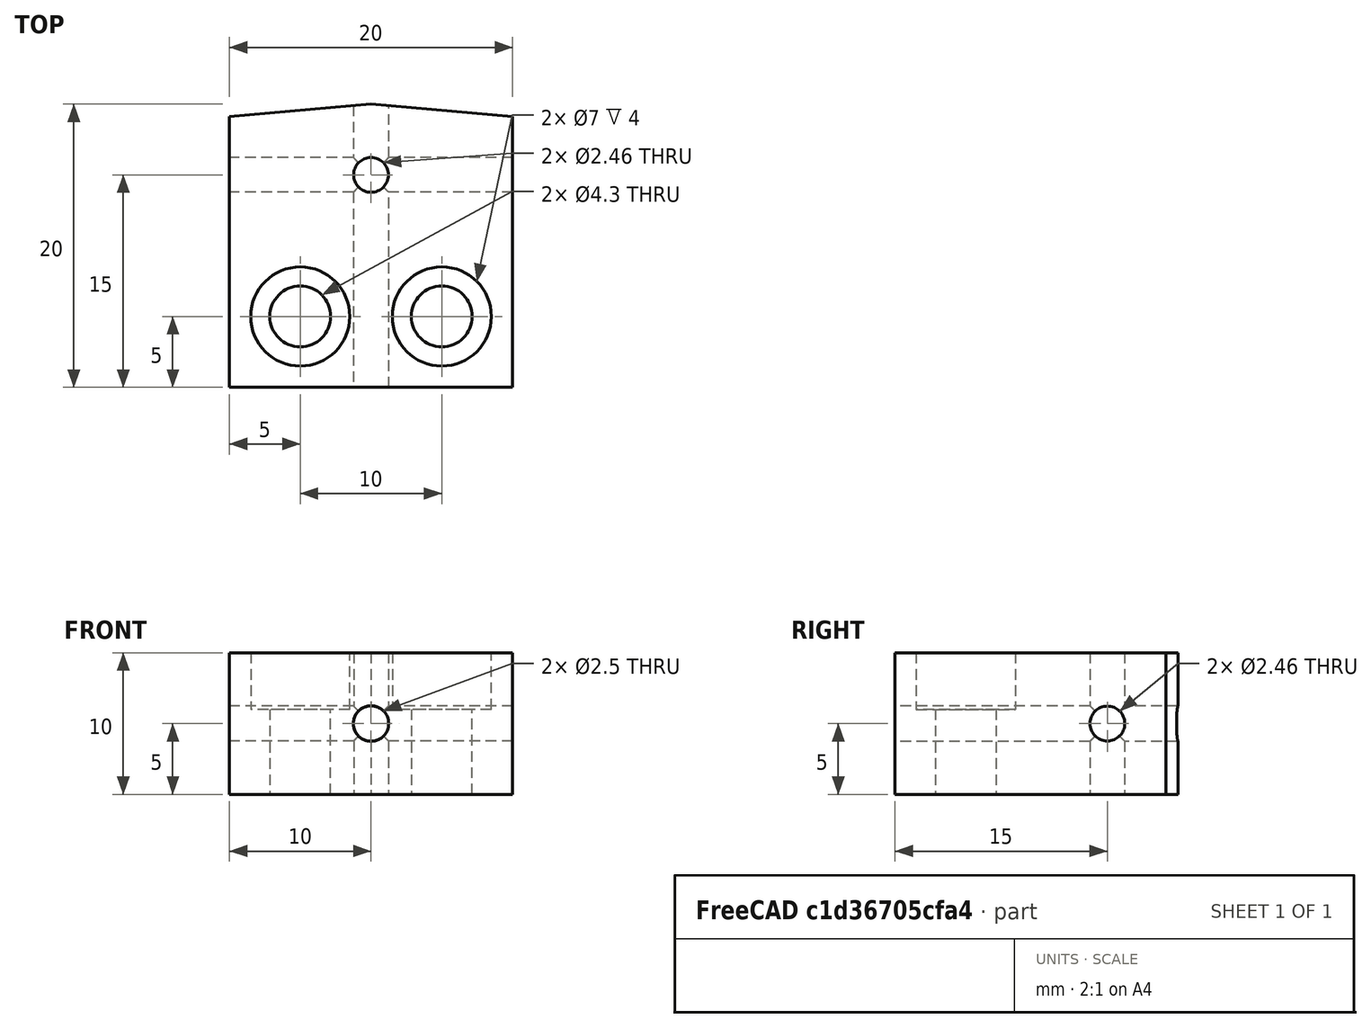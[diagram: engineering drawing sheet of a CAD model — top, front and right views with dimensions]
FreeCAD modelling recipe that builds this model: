
FCSTD DOCUMENT  (FreeCAD 0.21R0.21.2)
Label: StaticFiberFerruleMount_M4
License: All rights reserved
LicenseURL: https://en.wikipedia.org/wiki/All_rights_reserved
objects: TechDraw::DrawViewDimension×23, Part::Cylinder×5, Part::Cut×5, TechDraw::DrawProjGroupItem×5, Part::MultiFuse×4, Part::Box×3, TechDraw::DrawViewPart×3, TechDraw::DrawViewSection×3, Part::FeaturePython×2, TechDraw::DrawSVGTemplate×2, TechDraw::DrawPage×2, Part::Compound×1, TechDraw::DrawProjGroup×1
note: 56 computed .brp shape members not serialized (recipe doc carries the construction recipe); baked Part::Feature solids carry a one-line shape summary decoded from their .brp

FEATURE [Part::Box] Box  label="Cube"
  AttacherType = Attacher::AttachEngine3D
  Height = 10
  Length = 20
  Placement = pos=(-10,0,0) rot=(0,0,1;0rad)
  Width = 20
FEATURE [Part::Cylinder] Cylinder
  Angle = 360
  AttacherType = Attacher::AttachEngine3D
  FirstAngle = 0
  Height = 4
  Placement = pos=(0,0,6) rot=(0,0,1;0rad)
  Radius = 3.5
  SecondAngle = 0
FEATURE [Part::Cylinder] Cylinder001
  Angle = 360
  AttacherType = Attacher::AttachEngine3D
  FirstAngle = 0
  Height = 10
  Radius = 2.15
  SecondAngle = 0
FEATURE [Part::MultiFuse] Fusion
  Placement = pos=(-5,5,0) rot=(0,0,1;0rad)
  Shapes = -> [Cylinder001,Cylinder]
FEATURE [Part::Cylinder] Cylinder002
  Angle = 360
  AttacherType = Attacher::AttachEngine3D
  FirstAngle = 0
  Height = 4
  Placement = pos=(0,0,6) rot=(0,0,1;0rad)
  Radius = 3.5
  SecondAngle = 0
FEATURE [Part::Cylinder] Cylinder003
  Angle = 360
  AttacherType = Attacher::AttachEngine3D
  FirstAngle = 0
  Height = 10
  Radius = 2.15
  SecondAngle = 0
FEATURE [Part::MultiFuse] Fusion001
  Placement = pos=(5,5,0) rot=(0,0,1;0rad)
  Shapes = -> [Cylinder003,Cylinder002]
FEATURE [Part::MultiFuse] Fusion002
  Shapes = -> [Fusion,Fusion001]
FEATURE [Part::Cut] Cut
  Base = -> Box
  Tool = -> Fusion002
FEATURE [Part::Cylinder] Cylinder004
  Angle = 360
  AttacherType = Attacher::AttachEngine3D
  FirstAngle = 0
  Height = 20
  Placement = pos=(0,0,5) rot=(1,0,0;-1.5708rad)
  Radius = 1.25
  SecondAngle = 0
FEATURE [Part::Cut] Cut001
  Base = -> Cut
  Tool = -> Cylinder004
FEATURE [Part::FeaturePython] ScrewTap  label="M3x20-ScrewTap"  # Fasteners workbench fastener (typed FeaturePython)
  Placement = pos=(10,15,5) rot=(0,1,0;1.5708rad)
  diameter = 4
  diameterCustom = 20
  invert = false
  leftHanded = false
  length = 20
  matchOuter = false
  offset = 0
  pitchCustom = 1
  thread = false
  type = 2
FEATURE [Part::FeaturePython] ScrewTap001  label="M3x20-ScrewTap001"  # Fasteners workbench fastener (typed FeaturePython)
  Placement = pos=(0,15,15) rot=(0,1,0;0rad)
  diameter = 4
  diameterCustom = 20
  invert = false
  leftHanded = false
  length = 20
  matchOuter = false
  offset = 0
  pitchCustom = 1
  thread = false
  type = 2
FEATURE [Part::Cut] Cut002
  Base = -> Cut001
  Tool = -> ScrewTap
FEATURE [Part::Cut] Cut003
  Base = -> Cut002
  Tool = -> ScrewTap001
FEATURE [Part::Box] Box001  label="Cube001"
  AttacherType = Attacher::AttachEngine3D
  Height = 10
  Length = 15
  Placement = pos=(0,20,0) rot=(0,0,1;-0.087266rad)
  Width = 5
FEATURE [Part::Box] Box002  label="Cube002"
  AttacherType = Attacher::AttachEngine3D
  Height = 10
  Length = 15
  Placement = pos=(0,20,0) rot=(0,0,-1;0.087266rad)
  Width = 5
FEATURE [Part::Compound] Compound
  Links = -> [Box002]
  Placement = pos=(0,0,10) rot=(0,1,0;3.14159rad)
FEATURE [Part::MultiFuse] Fusion003
  Shapes = -> [Compound,Box001]
FEATURE [Part::Cut] Cut004  label="FiberMount"
  Base = -> Cut003
  Tool = -> Fusion003
FEATURE [TechDraw::DrawSVGTemplate] Template
  EditableTexts = Designed_by_Name=Thomas Spielauer; FC-Date=2024-01-30; FC-SC=mm; FC-Title=M4 Fiber Mount; Subtitle=For 2.5mm Ferrules
  Height = 210
  Orientation = 1
  Template = <path>
  Width = 297
FEATURE [TechDraw::DrawProjGroupItem] ProjItem  label="Front"
  CoarseView = false
  Direction = (0,0,1)
  Focus = 100
  HardHidden = false
  IsoCount = 0
  IsoHidden = false
  IsoVisible = false
  LockPosition = true
  Perspective = false
  Rotation = 0
  RotationVector = (-1,0,0)
  Scale = 2.5
  ScaleType = 2
  ScrubCount = 0
  SeamHidden = false
  SeamVisible = false
  SmoothHidden = false
  SmoothVisible = true
  Source = -> [Cut004]
  Type = 0
  X = 0
  XDirection = (-1,0,0)
  Y = 0
FEATURE [TechDraw::DrawProjGroupItem] ProjItem001  label="Left"
  CoarseView = false
  Direction = (1,0,1e-16)
  Focus = 100
  HardHidden = false
  IsoCount = 0
  IsoHidden = false
  IsoVisible = false
  LockPosition = false
  Perspective = false
  Rotation = 0
  RotationVector = (1,0,0)
  Scale = 2.5
  ScaleType = 2
  ScrubCount = 0
  SeamHidden = false
  SeamVisible = false
  SmoothHidden = false
  SmoothVisible = true
  Source = -> [Cut004]
  Type = 1
  X = 83.8051
  XDirection = (-1e-16,0,1)
  Y = 0
FEATURE [TechDraw::DrawProjGroupItem] ProjItem002  label="Rear"
  CoarseView = false
  Direction = (0,0,-1)
  Focus = 100
  HardHidden = false
  IsoCount = 0
  IsoHidden = false
  IsoVisible = false
  LockPosition = false
  Perspective = false
  Rotation = 0
  RotationVector = (1,0,0)
  Scale = 2.5
  ScaleType = 2
  ScrubCount = 0
  SeamHidden = false
  SeamVisible = false
  SmoothHidden = false
  SmoothVisible = true
  Source = -> [Cut004]
  Type = 3
  X = 176.998
  XDirection = (1,0,0)
  Y = 0
FEATURE [TechDraw::DrawProjGroupItem] ProjItem003  label="Top"
  CoarseView = false
  Direction = (0,-1,0)
  Focus = 100
  HardHidden = false
  IsoCount = 0
  IsoHidden = false
  IsoVisible = false
  LockPosition = false
  Perspective = false
  Rotation = 0
  RotationVector = (1,0,0)
  Scale = 2.5
  ScaleType = 2
  ScrubCount = 0
  SeamHidden = false
  SeamVisible = false
  SmoothHidden = false
  SmoothVisible = true
  Source = -> [Cut004]
  Type = 4
  X = 0
  XDirection = (-1,0,0)
  Y = -69.8299
FEATURE [TechDraw::DrawProjGroupItem] ProjItem004  label="Bottom"
  CoarseView = false
  Direction = (0,1,0)
  Focus = 100
  HardHidden = false
  IsoCount = 0
  IsoHidden = false
  IsoVisible = false
  LockPosition = false
  Perspective = false
  Rotation = 0
  RotationVector = (1,0,0)
  Scale = 2.5
  ScaleType = 2
  ScrubCount = 0
  SeamHidden = false
  SeamVisible = false
  SmoothHidden = false
  SmoothVisible = true
  Source = -> [Cut004]
  Type = 5
  X = 0
  XDirection = (-1,0,0)
  Y = 66.0072
FEATURE [TechDraw::DrawProjGroup] ProjGroup
  Anchor = -> ProjItem
  AutoDistribute = false
  LockPosition = false
  ProjectionType = 0
  Rotation = 0
  Scale = 2.5
  ScaleType = 2
  Source = -> [Cut004]
  Views = -> [ProjItem,ProjItem001,ProjItem002,ProjItem003,ProjItem004]
  X = 63.5172
  Y = 109.729
  spacingX = 15
  spacingY = 15
FEATURE [TechDraw::DrawViewDimension] Dimension
  AngleOverride = false
  Arbitrary = false
  ArbitraryTolerances = false
  EqualTolerance = true
  ExtensionAngle = 0
  FormatSpec = %.2w
  FormatSpecOverTolerance = %+.2w
  FormatSpecUnderTolerance = %+.2w
  Inverted = false
  LineAngle = 0
  LockPosition = false
  MeasureType = 1
  OverTolerance = 0
  References2D = -> [ProjItem002]
  Rotation = 0
  ScaleType = 0
  TheoreticalExact = false
  Type = 1
  UnderTolerance = 0
  X = -1.08718
  Y = 38.276
FEATURE [TechDraw::DrawViewDimension] Dimension001
  AngleOverride = false
  Arbitrary = false
  ArbitraryTolerances = false
  EqualTolerance = true
  ExtensionAngle = 0
  FormatSpec = %.2w
  FormatSpecOverTolerance = %+.2w
  FormatSpecUnderTolerance = %+.2w
  Inverted = false
  LineAngle = 0
  LockPosition = false
  MeasureType = 1
  OverTolerance = 0
  References2D = -> [ProjItem002]
  Rotation = 0
  ScaleType = 0
  TheoreticalExact = false
  Type = 2
  UnderTolerance = 0
  X = 33.6541
  Y = 3.92646
FEATURE [TechDraw::DrawViewDimension] Dimension002
  AngleOverride = false
  Arbitrary = false
  ArbitraryTolerances = false
  EqualTolerance = true
  ExtensionAngle = 0
  FormatSpec = %.2w
  FormatSpecOverTolerance = %+.2w
  FormatSpecUnderTolerance = %+.2w
  Inverted = false
  LineAngle = 0
  LockPosition = false
  MeasureType = 1
  OverTolerance = 0
  References2D = -> [ProjItem002]
  Rotation = 0
  ScaleType = 0
  TheoreticalExact = false
  Type = 1
  UnderTolerance = 0
  X = -19.3984
  Y = 49.6787
FEATURE [TechDraw::DrawViewDimension] Dimension003
  AngleOverride = false
  Arbitrary = false
  ArbitraryTolerances = false
  EqualTolerance = true
  ExtensionAngle = 0
  FormatSpec = %.2w
  FormatSpecOverTolerance = %+.2w
  FormatSpecUnderTolerance = %+.2w
  Inverted = false
  LineAngle = 0
  LockPosition = false
  MeasureType = 1
  OverTolerance = 0
  References2D = -> [ProjItem002]
  Rotation = 0
  ScaleType = 0
  TheoreticalExact = false
  Type = 1
  UnderTolerance = 0
  X = 18.4123
  Y = 48.3541
FEATURE [TechDraw::DrawViewDimension] Dimension004
  AngleOverride = false
  Arbitrary = false
  ArbitraryTolerances = false
  EqualTolerance = true
  ExtensionAngle = 0
  FormatSpec = %.2w
  FormatSpecOverTolerance = %+.2w
  FormatSpecUnderTolerance = %+.2w
  Inverted = false
  LineAngle = 0
  LockPosition = false
  MeasureType = 1
  OverTolerance = 0
  References2D = -> [ProjItem002]
  Rotation = 0
  ScaleType = 0
  TheoreticalExact = false
  Type = 2
  UnderTolerance = 0
  X = -36.9072
  Y = 21.9842
FEATURE [TechDraw::DrawViewDimension] Dimension005
  AngleOverride = false
  Arbitrary = false
  ArbitraryTolerances = false
  EqualTolerance = true
  ExtensionAngle = 0
  FormatSpec = %.2w
  FormatSpecOverTolerance = %+.2w
  FormatSpecUnderTolerance = %+.2w
  Inverted = false
  LineAngle = 0
  LockPosition = false
  MeasureType = 1
  OverTolerance = 0
  References2D = -> [ProjItem002]
  Rotation = 0
  ScaleType = 0
  TheoreticalExact = false
  Type = 2
  UnderTolerance = 0
  X = -49.4824
  Y = 5.98178
FEATURE [TechDraw::DrawViewDimension] Dimension006
  AngleOverride = false
  Arbitrary = false
  ArbitraryTolerances = false
  EqualTolerance = true
  ExtensionAngle = 0
  FormatSpec = %.2w
  FormatSpecOverTolerance = %+.2w
  FormatSpecUnderTolerance = %+.2w
  Inverted = false
  LineAngle = 0
  LockPosition = false
  MeasureType = 1
  OverTolerance = 0
  References2D = -> [ProjItem001]
  Rotation = 0
  ScaleType = 0
  TheoreticalExact = false
  Type = 2
  UnderTolerance = 0
  X = 20.9282
  Y = -0.08017
FEATURE [TechDraw::DrawViewDimension] Dimension007
  AngleOverride = false
  Arbitrary = false
  ArbitraryTolerances = false
  EqualTolerance = true
  ExtensionAngle = 0
  FormatSpec = %.2w
  FormatSpecOverTolerance = %+.2w
  FormatSpecUnderTolerance = %+.2w
  Inverted = false
  LineAngle = 0
  LockPosition = false
  MeasureType = 1
  OverTolerance = 0
  References2D = -> [ProjItem001]
  Rotation = 0
  ScaleType = 0
  TheoreticalExact = false
  Type = 1
  UnderTolerance = 0
  X = 1.11941
  Y = 39.7819
FEATURE [TechDraw::DrawViewDimension] Dimension008
  AngleOverride = false
  Arbitrary = false
  ArbitraryTolerances = false
  EqualTolerance = true
  ExtensionAngle = 0
  FormatSpec = %.2w
  FormatSpecOverTolerance = %+.2w
  FormatSpecUnderTolerance = %+.2w
  Inverted = false
  LineAngle = 0
  LockPosition = false
  MeasureType = 1
  OverTolerance = 0
  References2D = -> [ProjItem]
  Rotation = 0
  ScaleType = 0
  TheoreticalExact = false
  Type = 6
  UnderTolerance = 0
  X = 17.4114
  Y = -11.6712
FEATURE [TechDraw::DrawViewDimension] Dimension009
  AngleOverride = false
  Arbitrary = false
  ArbitraryTolerances = false
  EqualTolerance = true
  ExtensionAngle = 0
  FormatSpec = ⌀%.2w
  FormatSpecOverTolerance = %+.2w
  FormatSpecUnderTolerance = %+.2w
  Inverted = false
  LineAngle = 0
  LockPosition = false
  MeasureType = 1
  OverTolerance = 0
  References2D = -> [ProjItem]
  Rotation = 0
  ScaleType = 0
  TheoreticalExact = false
  Type = 5
  UnderTolerance = 0
  X = 34.847
  Y = 32.1835
FEATURE [TechDraw::DrawViewDimension] Dimension010
  AngleOverride = false
  Arbitrary = false
  ArbitraryTolerances = false
  EqualTolerance = true
  ExtensionAngle = 0
  FormatSpec = ⌀%.2w
  FormatSpecOverTolerance = %+.2w
  FormatSpecUnderTolerance = %+.2w
  Inverted = false
  LineAngle = 0
  LockPosition = false
  MeasureType = 1
  OverTolerance = 0
  References2D = -> [ProjItem]
  Rotation = 0
  ScaleType = 0
  TheoreticalExact = false
  Type = 5
  UnderTolerance = 0
  X = 42.735
  Y = 24.4512
FEATURE [TechDraw::DrawViewDimension] Dimension011
  AngleOverride = false
  Arbitrary = false
  ArbitraryTolerances = false
  EqualTolerance = true
  ExtensionAngle = 0
  FormatSpec = ⌀%.2w
  FormatSpecOverTolerance = %+.2w
  FormatSpecUnderTolerance = %+.2w
  Inverted = false
  LineAngle = 0
  LockPosition = false
  MeasureType = 1
  OverTolerance = 0
  References2D = -> [ProjItem003]
  Rotation = 0
  ScaleType = 0
  TheoreticalExact = false
  Type = 5
  UnderTolerance = 0
  X = 36.0608
  Y = 7.78296
FEATURE [TechDraw::DrawViewDimension] Dimension012
  AngleOverride = false
  Arbitrary = false
  ArbitraryTolerances = false
  EqualTolerance = true
  ExtensionAngle = 0
  FormatSpec = ⌀%.2w (M3)
  FormatSpecOverTolerance = %+.2w
  FormatSpecUnderTolerance = %+.2w
  Inverted = false
  LineAngle = 0
  LockPosition = false
  MeasureType = 1
  OverTolerance = 0
  References2D = -> [ProjItem]
  Rotation = 0
  ScaleType = 0
  TheoreticalExact = false
  Type = 5
  UnderTolerance = 0
  X = 47.6967
  Y = -20.8245
FEATURE [TechDraw::DrawViewDimension] Dimension013
  AngleOverride = false
  Arbitrary = false
  ArbitraryTolerances = false
  EqualTolerance = true
  ExtensionAngle = 0
  FormatSpec = ⌀%.2w (M3)
  FormatSpecOverTolerance = %+.2w
  FormatSpecUnderTolerance = %+.2w
  Inverted = false
  LineAngle = 0
  LockPosition = false
  MeasureType = 1
  OverTolerance = 0
  References2D = -> [ProjItem001]
  Rotation = 0
  ScaleType = 0
  TheoreticalExact = false
  Type = 5
  UnderTolerance = 0
  X = -33.134
  Y = 3.74181
FEATURE [TechDraw::DrawViewDimension] Dimension014
  AngleOverride = false
  Arbitrary = false
  ArbitraryTolerances = false
  EqualTolerance = true
  ExtensionAngle = 0
  FormatSpec = %.2w
  FormatSpecOverTolerance = %+.2w
  FormatSpecUnderTolerance = %+.2w
  Inverted = false
  LineAngle = 0
  LockPosition = false
  MeasureType = 1
  OverTolerance = 0
  References2D = -> [ProjItem004]
  Rotation = 0
  ScaleType = 0
  TheoreticalExact = false
  Type = 1
  UnderTolerance = 0
  X = 10.9437
  Y = -18.4908
FEATURE [TechDraw::DrawPage] Page
  KeepUpdated = true
  NextBalloonIndex = 1
  ProjectionType = 0
  Template = -> Template
  Views = -> [ProjGroup,Dimension,Dimension001,Dimension002,Dimension003,Dimension004,Dimension005,Dimension006,Dimension007,Dimension008,Dimension009,Dimension010,Dimension011,Dimension012,Dimension013,Dimension014]
FEATURE [TechDraw::DrawSVGTemplate] Template001
  EditableTexts = Designed_by_Name=Thomas Spielauer; FC-Date=2024-01-30; FC-SC=mm; FC-SH=2/2; FC-Title=M4 Fiber Mount; Subtitle=For 2.5mm fiber ferrules
  Height = 210
  Orientation = 1
  Template = <path>
  Width = 297
FEATURE [TechDraw::DrawViewPart] View
  CoarseView = false
  Direction = (0,0,1)
  Focus = 100
  HardHidden = false
  IsoCount = 0
  IsoHidden = false
  IsoVisible = false
  LockPosition = false
  Perspective = false
  Rotation = 0
  Scale = 2
  ScaleType = 2
  ScrubCount = 0
  SeamHidden = false
  SeamVisible = false
  SmoothHidden = false
  SmoothVisible = true
  Source = -> [Cut004]
  X = 49.0155
  XDirection = (-1,0,0)
  Y = 162
FEATURE [TechDraw::DrawViewSection] SectionView  label="Section  - "
  BaseView = -> View
  CoarseView = false
  CutSurfaceDisplay = 2
  Direction = (1,1e-16,0)
  FileGeomPattern = <path>
  FileHatchPattern = <path>
  Focus = 100
  FuseBeforeCut = false
  HardHidden = false
  HatchOffset = (0,0,0)
  HatchRotation = 0
  HatchScale = 1
  IsoCount = 0
  IsoHidden = false
  IsoVisible = false
  LockPosition = false
  NameGeomPattern = Diamond
  Perspective = false
  Rotation = -90
  Scale = 2
  ScaleType = 2
  ScrubCount = 0
  SeamHidden = false
  SeamVisible = false
  SectionDirection = 4
  SectionNormal = (1,1e-16,0)
  SectionOrigin = (0,10,5)
  SmoothHidden = false
  SmoothVisible = true
  Source = -> [Cut004]
  TrimAfterCut = false
  X = 98.3829
  XDirection = (-1e-16,1,0)
  Y = 161.597
FEATURE [TechDraw::DrawViewPart] View001
  CoarseView = false
  Direction = (0,0,1)
  Focus = 100
  HardHidden = false
  IsoCount = 0
  IsoHidden = false
  IsoVisible = false
  LockPosition = false
  Perspective = false
  Rotation = 0
  Scale = 2
  ScaleType = 2
  ScrubCount = 0
  SeamHidden = false
  SeamVisible = false
  SmoothHidden = false
  SmoothVisible = true
  Source = -> [Cut004]
  X = 168.995
  XDirection = (-1,0,0)
  Y = 161.465
FEATURE [TechDraw::DrawViewSection] SectionView001  label="Section  - 001"
  BaseView = -> View001
  CoarseView = false
  CutSurfaceDisplay = 2
  Direction = (1,1e-16,0)
  FileGeomPattern = <path>
  FileHatchPattern = <path>
  Focus = 100
  FuseBeforeCut = false
  HardHidden = false
  HatchOffset = (0,0,0)
  HatchRotation = 0
  HatchScale = 1
  IsoCount = 0
  IsoHidden = false
  IsoVisible = false
  LockPosition = false
  NameGeomPattern = Diamond
  Perspective = false
  Rotation = -90
  Scale = 2
  ScaleType = 2
  ScrubCount = 0
  SeamHidden = false
  SeamVisible = false
  SectionDirection = 4
  SectionNormal = (1,1e-16,0)
  SectionOrigin = (5,10,5)
  SmoothHidden = false
  SmoothVisible = true
  Source = -> [Cut004]
  TrimAfterCut = false
  X = 225.041
  XDirection = (-1e-16,1,0)
  Y = 158.119
FEATURE [TechDraw::DrawViewDimension] Dimension015
  AngleOverride = false
  Arbitrary = false
  ArbitraryTolerances = false
  EqualTolerance = true
  ExtensionAngle = 0
  FormatSpec = %.2w
  FormatSpecOverTolerance = %+.2w
  FormatSpecUnderTolerance = %+.2w
  Inverted = false
  LineAngle = 0
  LockPosition = false
  MeasureType = 1
  OverTolerance = 0
  References2D = -> [SectionView]
  Rotation = 0
  ScaleType = 0
  TheoreticalExact = false
  Type = 1
  UnderTolerance = 0
  X = 9.95348
  Y = -24.9456
FEATURE [TechDraw::DrawViewDimension] Dimension016
  AngleOverride = false
  Arbitrary = false
  ArbitraryTolerances = false
  EqualTolerance = true
  ExtensionAngle = 0
  FormatSpec = %.2w (M3)
  FormatSpecOverTolerance = %+.2w
  FormatSpecUnderTolerance = %+.2w
  Inverted = false
  LineAngle = 0
  LockPosition = false
  MeasureType = 1
  OverTolerance = 0
  References2D = -> [SectionView]
  Rotation = 0
  ScaleType = 0
  TheoreticalExact = false
  Type = 2
  UnderTolerance = 0
  X = 17.8961
  Y = 1.78628
FEATURE [TechDraw::DrawViewDimension] Dimension017
  AngleOverride = false
  Arbitrary = false
  ArbitraryTolerances = false
  EqualTolerance = true
  ExtensionAngle = 0
  FormatSpec = %.2w
  FormatSpecOverTolerance = %+.2w
  FormatSpecUnderTolerance = %+.2w
  Inverted = false
  LineAngle = 0
  LockPosition = false
  MeasureType = 1
  OverTolerance = 0
  References2D = -> [SectionView001]
  Rotation = 0
  ScaleType = 0
  TheoreticalExact = false
  Type = 2
  UnderTolerance = 0
  X = 19.2955
  Y = 12.763
FEATURE [TechDraw::DrawViewDimension] Dimension018
  AngleOverride = false
  Arbitrary = false
  ArbitraryTolerances = false
  EqualTolerance = true
  ExtensionAngle = 0
  FormatSpec = %.2w
  FormatSpecOverTolerance = %+.2w
  FormatSpecUnderTolerance = %+.2w
  Inverted = false
  LineAngle = 0
  LockPosition = false
  MeasureType = 1
  OverTolerance = 0
  References2D = -> [SectionView001]
  Rotation = 0
  ScaleType = 0
  TheoreticalExact = false
  Type = 2
  UnderTolerance = 0
  X = -21.1185
  Y = 11.8913
FEATURE [TechDraw::DrawViewDimension] Dimension019
  AngleOverride = false
  Arbitrary = false
  ArbitraryTolerances = false
  EqualTolerance = true
  ExtensionAngle = 0
  FormatSpec = %.2w
  FormatSpecOverTolerance = %+.2w
  FormatSpecUnderTolerance = %+.2w
  Inverted = false
  LineAngle = 0
  LockPosition = false
  MeasureType = 1
  OverTolerance = 0
  References2D = -> [SectionView001]
  Rotation = 0
  ScaleType = 0
  TheoreticalExact = false
  Type = 1
  UnderTolerance = 0
  X = 5.85417
  Y = 33.4173
FEATURE [TechDraw::DrawViewDimension] Dimension020
  AngleOverride = false
  Arbitrary = false
  ArbitraryTolerances = false
  EqualTolerance = true
  ExtensionAngle = 0
  FormatSpec = %.2w
  FormatSpecOverTolerance = %+.2w
  FormatSpecUnderTolerance = %+.2w
  Inverted = false
  LineAngle = 0
  LockPosition = false
  MeasureType = 1
  OverTolerance = 0
  References2D = -> [SectionView001]
  Rotation = 0
  ScaleType = 0
  TheoreticalExact = false
  Type = 1
  UnderTolerance = 0
  X = -4.51158
  Y = 40.6578
FEATURE [TechDraw::DrawViewPart] View002
  CoarseView = false
  Direction = (0,0,1)
  Focus = 100
  HardHidden = false
  IsoCount = 0
  IsoHidden = false
  IsoVisible = false
  LockPosition = false
  Perspective = false
  Rotation = 90
  Scale = 2
  ScaleType = 2
  ScrubCount = 0
  SeamHidden = false
  SeamVisible = false
  SmoothHidden = false
  SmoothVisible = true
  Source = -> [Cut004]
  X = 44.9676
  XDirection = (-1,0,0)
  Y = 66.078
FEATURE [TechDraw::DrawViewSection] SectionView002  label="Section  - 002"
  BaseView = -> View002
  CoarseView = false
  CutSurfaceDisplay = 2
  Direction = (-1e-16,-1,0)
  FileGeomPattern = <path>
  FileHatchPattern = <path>
  Focus = 100
  FuseBeforeCut = false
  HardHidden = false
  HatchOffset = (0,0,0)
  HatchRotation = 0
  HatchScale = 1
  IsoCount = 0
  IsoHidden = false
  IsoVisible = false
  LockPosition = false
  NameGeomPattern = Diamond
  Perspective = false
  Rotation = 90
  Scale = 2
  ScaleType = 2
  ScrubCount = 0
  SeamHidden = false
  SeamVisible = false
  SectionDirection = 4
  SectionNormal = (-1e-16,-1,0)
  SectionOrigin = (0,15,5)
  SmoothHidden = false
  SmoothVisible = true
  Source = -> [Cut004]
  TrimAfterCut = false
  X = 99.4341
  XDirection = (-1,1e-16,0)
  Y = 66.7295
FEATURE [TechDraw::DrawViewDimension] Dimension021
  AngleOverride = false
  Arbitrary = false
  ArbitraryTolerances = false
  EqualTolerance = true
  ExtensionAngle = 0
  FormatSpec = %.2w (M3)
  FormatSpecOverTolerance = %+.2w
  FormatSpecUnderTolerance = %+.2w
  Inverted = false
  LineAngle = 0
  LockPosition = false
  MeasureType = 1
  OverTolerance = 0
  References2D = -> [SectionView002]
  Rotation = 0
  ScaleType = 0
  TheoreticalExact = false
  Type = 1
  UnderTolerance = 0
  X = 6.54939
  Y = 38.4283
FEATURE [TechDraw::DrawViewDimension] Dimension022
  AngleOverride = false
  Arbitrary = false
  ArbitraryTolerances = false
  EqualTolerance = true
  ExtensionAngle = 0
  FormatSpec = %.2w (M3)
  FormatSpecOverTolerance = %+.2w
  FormatSpecUnderTolerance = %+.2w
  Inverted = false
  LineAngle = 0
  LockPosition = false
  MeasureType = 1
  OverTolerance = 0
  References2D = -> [SectionView002]
  Rotation = 0
  ScaleType = 0
  TheoreticalExact = false
  Type = 2
  UnderTolerance = 0
  X = 32.8643
  Y = 22.8736
FEATURE [TechDraw::DrawPage] Page001
  KeepUpdated = true
  NextBalloonIndex = 1
  ProjectionType = 0
  Template = -> Template001
  Views = -> [View,SectionView,View001,SectionView001,Dimension015,Dimension016,Dimension017,Dimension018,Dimension019,Dimension020,View002,SectionView002,Dimension021,Dimension022]
note: 8 file-system paths scrubbed to <path> (originals preserved in the JSON sidecar)
